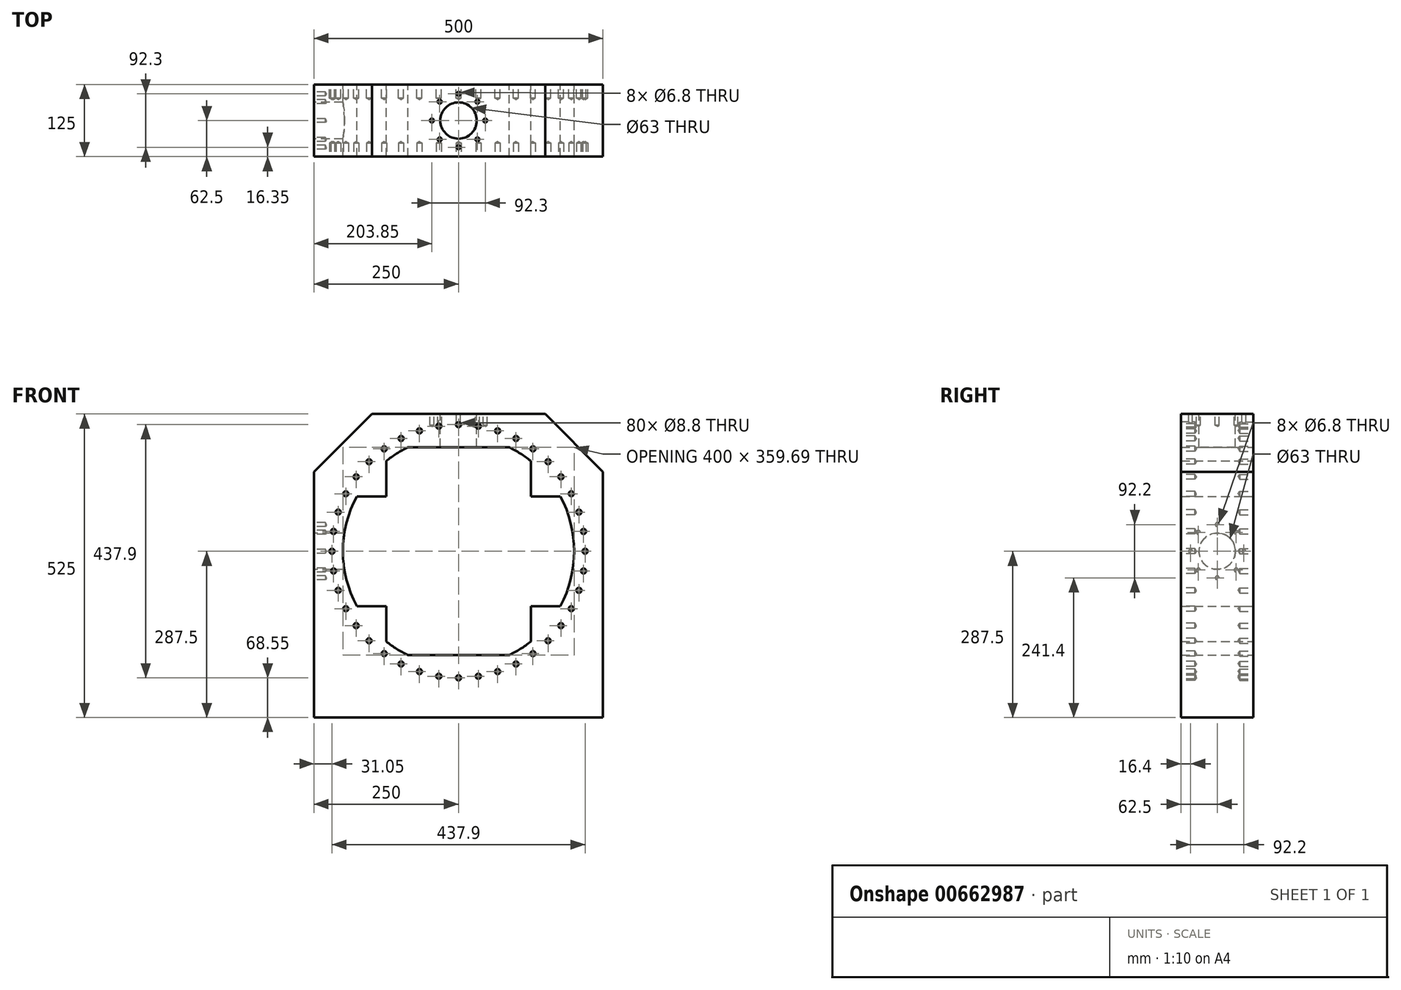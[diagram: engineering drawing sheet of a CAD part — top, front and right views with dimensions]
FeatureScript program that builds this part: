
annotation { "Feature Type Name" : "Feature", "Feature Type Description" : "" }
export const myFeature = defineFeature(function(context is Context, id is Id, definition is map)
    precondition{}
    {
        {
            var Q0;
            Q0=qCreatedBy(makeId("Front.planeOp"),FACE);
            var sketch = newSketch(context, id + "F0", { "sketchPlane" : qUnion([Q0])});
            skPoint(sketch, "E0.middle", {"position": v(0, 0) * mm});
            skLineSegment(sketch, "E1.bottom", {"start": v(250, -287.5) * mm, "end": v(-250, -287.5) * mm});
            skLineSegment(sketch, "E1.top", {"start": v(250, 237.5) * mm, "end": v(-250, 237.5) * mm});
            skLineSegment(sketch, "E1.left", {"start": v(250, -287.5) * mm, "end": v(250, 237.5) * mm});
            skLineSegment(sketch, "E1.right", {"start": v(-250, -287.5) * mm, "end": v(-250, 237.5) * mm});
            skPoint(sketch, "E1.middle", {"position": v(0, -25) * mm});
            skCircle(sketch, "E2", {"center": v(0, 0) * mm, "radius": 235 * mm, "construction": true});
            skLineSegment(sketch, "E3", {"start": v(0, 200) * mm, "end": v(0, -200) * mm, "construction": true});
            skLineSegment(sketch, "E4", {"start": v(-176, 95) * mm, "end": v(-125, 95) * mm});
            skLineSegment(sketch, "E5", {"start": v(-125, 95) * mm, "end": v(-125, 156.12) * mm});
            skLineSegment(sketch, "E6", {"start": v(-125, -95) * mm, "end": v(-176, -95) * mm});
            skLineSegment(sketch, "E7", {"start": v(176, 95) * mm, "end": v(125, 95) * mm});
            skLineSegment(sketch, "E8", {"start": v(125, 95) * mm, "end": v(125, 156.12) * mm});
            skLineSegment(sketch, "E9", {"start": v(176, -95) * mm, "end": v(125, -95) * mm});
            skLineSegment(sketch, "E10", {"start": v(125, -95) * mm, "end": v(125, -156.12) * mm});
            skArc(sketch, "E11", {"start": v(176, 95) * mm, "mid": v(153.57, 128.13) * mm, "end": v(125, 156.12) * mm, "construction": true});
            skArc(sketch, "E12", {"start": v(176, -95) * mm, "mid": v(200, 0) * mm, "end": v(176, 95) * mm});
            skArc(sketch, "E13", {"start": v(125, 156.12) * mm, "mid": v(106.9, 169.03) * mm, "end": v(87.5, 179.84) * mm});
            skArc(sketch, "E14", {"start": v(-125, 156.12) * mm, "mid": v(-153.57, 128.13) * mm, "end": v(-176, 95) * mm, "construction": true});
            skArc(sketch, "E15", {"start": v(-176, 95) * mm, "mid": v(-200, 0) * mm, "end": v(-176, -95) * mm});
            skArc(sketch, "E16", {"start": v(-176, -95) * mm, "mid": v(-153.57, -128.13) * mm, "end": v(-125, -156.12) * mm, "construction": true});
            skLineSegment(sketch, "E17", {"start": v(-87.5, 179.84) * mm, "end": v(87.5, 179.84) * mm});
            skArc(sketch, "E18", {"start": v(-87.5, 179.84) * mm, "mid": v(-106.9, 169.03) * mm, "end": v(-125, 156.12) * mm});
            skLineSegment(sketch, "E19", {"start": v(87.5, 179.84) * mm, "end": v(87.5, 179.84) * mm});
            skArc(sketch, "E20", {"start": v(87.5, 179.84) * mm, "mid": v(0, 200) * mm, "end": v(-87.5, 179.84) * mm, "construction": true});
            skCircle(sketch, "E21", {"center": v(0, 0) * mm, "radius": 218.95 * mm, "construction": true});
            skLineSegment(sketch, "E22", {"start": v(-125, -95) * mm, "end": v(-125, -156.12) * mm});
            skLineSegment(sketch, "E23", {"start": v(-125, -156.12) * mm, "end": v(125, -156.12) * mm, "construction": true});
            skLineSegment(sketch, "E24", {"start": v(-87.5, -179.84) * mm, "end": v(87.5, -179.84) * mm});
            skArc(sketch, "E25", {"start": v(-87.5, -179.84) * mm, "mid": v(0, -200) * mm, "end": v(87.5, -179.84) * mm, "construction": true});
            skArc(sketch, "E26", {"start": v(-125, -156.12) * mm, "mid": v(-106.9, -169.03) * mm, "end": v(-87.5, -179.84) * mm});
            skLineSegment(sketch, "E27", {"start": v(87.5, -179.84) * mm, "end": v(87.5, -179.84) * mm});
            skLineSegment(sketch, "E28", {"start": v(125, -156.12) * mm, "end": v(125, -156.12) * mm});
            skArc(sketch, "E29", {"start": v(87.5, -179.84) * mm, "mid": v(106.9, -169.03) * mm, "end": v(125, -156.12) * mm});
            skPoint(sketch, "E30", {"position": v(218.95, 0) * mm});
            skLineSegment(sketch, "E31", {"start": v(0, 0) * mm, "end": v(218.95, 0) * mm, "construction": true});
            skPoint(sketch, "E32.1.0", {"position": v(216.25, 34.25) * mm});
            skPoint(sketch, "E32.2.0", {"position": v(208.23, 67.66) * mm});
            skPoint(sketch, "E32.3.0", {"position": v(195.09, 99.4) * mm});
            skPoint(sketch, "E32.4.0", {"position": v(177.13, 128.7) * mm});
            skPoint(sketch, "E32.5.0", {"position": v(154.82, 154.82) * mm});
            skPoint(sketch, "E32.6.0", {"position": v(128.7, 177.13) * mm});
            skPoint(sketch, "E32.7.0", {"position": v(99.4, 195.09) * mm});
            skPoint(sketch, "E32.8.0", {"position": v(67.66, 208.23) * mm});
            skPoint(sketch, "E32.9.0", {"position": v(34.25, 216.25) * mm});
            skPoint(sketch, "E32.10.0", {"position": v(0, 218.95) * mm});
            skPoint(sketch, "E32.11.0", {"position": v(-34.25, 216.25) * mm});
            skPoint(sketch, "E32.12.0", {"position": v(-67.66, 208.23) * mm});
            skPoint(sketch, "E32.13.0", {"position": v(-99.4, 195.09) * mm});
            skPoint(sketch, "E32.14.0", {"position": v(-128.7, 177.13) * mm});
            skPoint(sketch, "E32.15.0", {"position": v(-154.82, 154.82) * mm});
            skPoint(sketch, "E32.16.0", {"position": v(-177.13, 128.7) * mm});
            skPoint(sketch, "E32.17.0", {"position": v(-195.09, 99.4) * mm});
            skPoint(sketch, "E32.18.0", {"position": v(-208.23, 67.66) * mm});
            skPoint(sketch, "E32.19.0", {"position": v(-216.25, 34.25) * mm});
            skPoint(sketch, "E32.20.0", {"position": v(-218.95, 0) * mm});
            skPoint(sketch, "E32.21.0", {"position": v(-216.25, -34.25) * mm});
            skPoint(sketch, "E32.22.0", {"position": v(-208.23, -67.66) * mm});
            skPoint(sketch, "E32.23.0", {"position": v(-195.09, -99.4) * mm});
            skPoint(sketch, "E32.24.0", {"position": v(-177.13, -128.7) * mm});
            skPoint(sketch, "E32.25.0", {"position": v(-154.82, -154.82) * mm});
            skPoint(sketch, "E32.26.0", {"position": v(-128.7, -177.13) * mm});
            skPoint(sketch, "E32.27.0", {"position": v(-99.4, -195.09) * mm});
            skPoint(sketch, "E32.28.0", {"position": v(-67.66, -208.23) * mm});
            skPoint(sketch, "E32.29.0", {"position": v(-34.25, -216.25) * mm});
            skPoint(sketch, "E32.30.0", {"position": v(0, -218.95) * mm});
            skPoint(sketch, "E32.31.0", {"position": v(34.25, -216.25) * mm});
            skPoint(sketch, "E32.32.0", {"position": v(67.66, -208.23) * mm});
            skPoint(sketch, "E32.33.0", {"position": v(99.4, -195.09) * mm});
            skPoint(sketch, "E32.34.0", {"position": v(128.7, -177.13) * mm});
            skPoint(sketch, "E32.35.0", {"position": v(154.82, -154.82) * mm});
            skPoint(sketch, "E32.36.0", {"position": v(177.13, -128.7) * mm});
            skPoint(sketch, "E32.37.0", {"position": v(195.09, -99.4) * mm});
            skPoint(sketch, "E32.38.0", {"position": v(208.23, -67.66) * mm});
            skPoint(sketch, "E32.39.0", {"position": v(216.25, -34.25) * mm});
            skSolve(sketch);
        }
        {
            var Q0;
            Q0=makeQuery(id+"F0.imprint","IMPRINT",FACE,{"disambiguationData":[TD([[makeQuery(id+"F0.imprint","IMPRINT",EDGE,{"derivedFrom":sQuery(id+"F0.wireOp",EDGE,"E1.bottom")}),-1.0]])]});
            extrude(context, id + "F1", {"entities" : qUnion([Q0]), "depth" : 125 * mm, "offsetDistance" : 25 * mm});
        }
        {
            var Q0;
            Q0=sQuery(id+"F0.wireOp",VERTEX,"E32.20.0");
            var Q1;
            Q1=sQuery(id+"F0.wireOp",VERTEX,"E32.19.0");
            var Q2;
            Q2=sQuery(id+"F0.wireOp",VERTEX,"E32.18.0");
            var Q3;
            Q3=sQuery(id+"F0.wireOp",VERTEX,"E32.17.0");
            var Q4;
            Q4=sQuery(id+"F0.wireOp",VERTEX,"E32.16.0");
            var Q5;
            Q5=sQuery(id+"F0.wireOp",VERTEX,"E32.15.0");
            var Q6;
            Q6=sQuery(id+"F0.wireOp",VERTEX,"E32.14.0");
            var Q7;
            Q7=sQuery(id+"F0.wireOp",VERTEX,"E32.13.0");
            var Q8;
            Q8=sQuery(id+"F0.wireOp",VERTEX,"E32.12.0");
            var Q9;
            Q9=sQuery(id+"F0.wireOp",VERTEX,"E32.11.0");
            var Q10;
            Q10=sQuery(id+"F0.wireOp",VERTEX,"E32.10.0");
            var Q11;
            Q11=sQuery(id+"F0.wireOp",VERTEX,"E32.9.0");
            var Q12;
            Q12=sQuery(id+"F0.wireOp",VERTEX,"E32.8.0");
            var Q13;
            Q13=sQuery(id+"F0.wireOp",VERTEX,"E32.7.0");
            var Q14;
            Q14=sQuery(id+"F0.wireOp",VERTEX,"E32.6.0");
            var Q15;
            Q15=sQuery(id+"F0.wireOp",VERTEX,"E32.5.0");
            var Q16;
            Q16=sQuery(id+"F0.wireOp",VERTEX,"E32.4.0");
            var Q17;
            Q17=sQuery(id+"F0.wireOp",VERTEX,"E32.3.0");
            var Q18;
            Q18=sQuery(id+"F0.wireOp",VERTEX,"E32.2.0");
            var Q19;
            Q19=sQuery(id+"F0.wireOp",VERTEX,"E32.1.0");
            var Q20;
            Q20=sQuery(id+"F0.wireOp",VERTEX,"E30");
            var Q21;
            Q21=sQuery(id+"F0.wireOp",VERTEX,"E32.39.0");
            var Q22;
            Q22=sQuery(id+"F0.wireOp",VERTEX,"E32.38.0");
            var Q23;
            Q23=sQuery(id+"F0.wireOp",VERTEX,"E32.37.0");
            var Q24;
            Q24=sQuery(id+"F0.wireOp",VERTEX,"E32.36.0");
            var Q25;
            Q25=sQuery(id+"F0.wireOp",VERTEX,"E32.35.0");
            var Q26;
            Q26=sQuery(id+"F0.wireOp",VERTEX,"E32.34.0");
            var Q27;
            Q27=sQuery(id+"F0.wireOp",VERTEX,"E32.33.0");
            var Q28;
            Q28=sQuery(id+"F0.wireOp",VERTEX,"E32.32.0");
            var Q29;
            Q29=sQuery(id+"F0.wireOp",VERTEX,"E32.31.0");
            var Q30;
            Q30=sQuery(id+"F0.wireOp",VERTEX,"E32.30.0");
            var Q31;
            Q31=sQuery(id+"F0.wireOp",VERTEX,"E32.29.0");
            var Q32;
            Q32=sQuery(id+"F0.wireOp",VERTEX,"E32.28.0");
            var Q33;
            Q33=sQuery(id+"F0.wireOp",VERTEX,"E32.27.0");
            var Q34;
            Q34=sQuery(id+"F0.wireOp",VERTEX,"E32.26.0");
            var Q35;
            Q35=sQuery(id+"F0.wireOp",VERTEX,"E32.25.0");
            var Q36;
            Q36=sQuery(id+"F0.wireOp",VERTEX,"E32.24.0");
            var Q37;
            Q37=sQuery(id+"F0.wireOp",VERTEX,"E32.23.0");
            var Q38;
            Q38=sQuery(id+"F0.wireOp",VERTEX,"E32.22.0");
            var Q39;
            Q39=sQuery(id+"F0.wireOp",VERTEX,"E32.21.0");
            var Q40;
            Q40=makeQuery(id+"F1.opExtrude","SWEPT_BODY",BODY,{"disambiguationData":[OSD([sQuery(id+"F0.wireOp",EDGE,"E1.bottom"),sQuery(id+"F0.wireOp",EDGE,"E1.top"),sQuery(id+"F0.wireOp",EDGE,"E1.left"),sQuery(id+"F0.wireOp",EDGE,"E1.right"),sQuery(id+"F0.wireOp",EDGE,"E4"),sQuery(id+"F0.wireOp",EDGE,"E5"),sQuery(id+"F0.wireOp",EDGE,"E6"),sQuery(id+"F0.wireOp",EDGE,"E7"),sQuery(id+"F0.wireOp",EDGE,"E8"),sQuery(id+"F0.wireOp",EDGE,"E9"),sQuery(id+"F0.wireOp",EDGE,"E10"),sQuery(id+"F0.wireOp",EDGE,"E12"),sQuery(id+"F0.wireOp",EDGE,"E13"),sQuery(id+"F0.wireOp",EDGE,"E15"),sQuery(id+"F0.wireOp",EDGE,"E17"),sQuery(id+"F0.wireOp",EDGE,"E18"),sQuery(id+"F0.wireOp",EDGE,"E22"),sQuery(id+"F0.wireOp",EDGE,"E24"),sQuery(id+"F0.wireOp",EDGE,"E26"),sQuery(id+"F0.wireOp",EDGE,"E29")])]});
            hole(context, id + "F2", {"style" : HoleStyle.SIMPLE, "endStyle" : HoleEndStyle.BLIND, "oppositeDirection" : true, "standardTappedOrClearance" : lookupTablePath({ "standard" : "ISO", "engagement" : "75%", "pitch" : "1.25 mm", "size" : "M10", "type" : "Tapped" }), "standardBlindInLast" : lookupTablePath({ "standard" : "ISO", "fit" : "Normal", "engagement" : "75%", "pitch" : "1.25 mm", "size" : "M10", "type" : "Clearance & tapped" }), "holeDiameter" : 8.8 * mm, "majorDiameter" : 10 * mm, "showTappedDepth" : true, "holeDepth" : 23.75 * mm, "isTappedThrough" : true, "tappedDepth" : 20 * mm, "tapClearance" : 3, "locations" : qUnion([Q0, Q1, Q2, Q3, Q4, Q5, Q6, Q7, Q8, Q9, Q10, Q11, Q12, Q13, Q14, Q15, Q16, Q17, Q18, Q19, Q20, Q21, Q22, Q23, Q24, Q25, Q26, Q27, Q28, Q29, Q30, Q31, Q32, Q33, Q34, Q35, Q36, Q37, Q38, Q39]), "scope" : qUnion([Q40])});
        }
        {
            var Q0;
            Q0=makeQuery(id+"F1.opExtrude","SWEPT_EDGE",EDGE,{"disambiguationData":[OSD([sQuery(id+"F0.wireOp",EDGE,"E1.top"),sQuery(id+"F0.wireOp",EDGE,"E1.right")])]});
            var Q1;
            Q1=makeQuery(id+"F1.opExtrude","SWEPT_EDGE",EDGE,{"disambiguationData":[OSD([sQuery(id+"F0.wireOp",EDGE,"E1.top"),sQuery(id+"F0.wireOp",EDGE,"E1.left")])]});
            chamfer(context, id + "F3", {"entities" : qUnion([Q0, Q1]), "width" : 100 * mm, "tangentPropagation" : true});
        }
        {
            var Q0;
            Q0=makeQuery(id+"F1.opExtrude","CAP_FACE",FACE,{"disambiguationData":[OSD([sQuery(id+"F0.wireOp",EDGE,"E1.bottom"),sQuery(id+"F0.wireOp",EDGE,"E1.top"),sQuery(id+"F0.wireOp",EDGE,"E1.left"),sQuery(id+"F0.wireOp",EDGE,"E1.right"),sQuery(id+"F0.wireOp",EDGE,"E4"),sQuery(id+"F0.wireOp",EDGE,"E5"),sQuery(id+"F0.wireOp",EDGE,"E6"),sQuery(id+"F0.wireOp",EDGE,"E7"),sQuery(id+"F0.wireOp",EDGE,"E8"),sQuery(id+"F0.wireOp",EDGE,"E9"),sQuery(id+"F0.wireOp",EDGE,"E10"),sQuery(id+"F0.wireOp",EDGE,"E12"),sQuery(id+"F0.wireOp",EDGE,"E13"),sQuery(id+"F0.wireOp",EDGE,"E15"),sQuery(id+"F0.wireOp",EDGE,"E17"),sQuery(id+"F0.wireOp",EDGE,"E18"),sQuery(id+"F0.wireOp",EDGE,"E22"),sQuery(id+"F0.wireOp",EDGE,"E24"),sQuery(id+"F0.wireOp",EDGE,"E26"),sQuery(id+"F0.wireOp",EDGE,"E29")])],"isStart":false});
            var sketch = newSketch(context, id + "F4", { "sketchPlane" : qUnion([Q0])});
            skCircle(sketch, "E33", {"center": v(0, 0) * mm, "radius": 218.95 * mm, "construction": true});
            skPoint(sketch, "E34", {"position": v(218.95, 0) * mm});
            skLineSegment(sketch, "E35", {"start": v(0, 0) * mm, "end": v(218.95, 0) * mm, "construction": true});
            skPoint(sketch, "E36.1.0", {"position": v(216.25, 34.25) * mm});
            skPoint(sketch, "E36.2.0", {"position": v(208.23, 67.66) * mm});
            skPoint(sketch, "E36.3.0", {"position": v(195.09, 99.4) * mm});
            skPoint(sketch, "E36.4.0", {"position": v(177.13, 128.7) * mm});
            skPoint(sketch, "E36.5.0", {"position": v(154.82, 154.82) * mm});
            skPoint(sketch, "E36.6.0", {"position": v(128.7, 177.13) * mm});
            skPoint(sketch, "E36.7.0", {"position": v(99.4, 195.09) * mm});
            skPoint(sketch, "E36.8.0", {"position": v(67.66, 208.23) * mm});
            skPoint(sketch, "E36.9.0", {"position": v(34.25, 216.25) * mm});
            skPoint(sketch, "E36.10.0", {"position": v(0, 218.95) * mm});
            skPoint(sketch, "E36.11.0", {"position": v(-34.25, 216.25) * mm});
            skPoint(sketch, "E36.12.0", {"position": v(-67.66, 208.23) * mm});
            skPoint(sketch, "E36.13.0", {"position": v(-99.4, 195.09) * mm});
            skPoint(sketch, "E36.14.0", {"position": v(-128.7, 177.13) * mm});
            skPoint(sketch, "E36.15.0", {"position": v(-154.82, 154.82) * mm});
            skPoint(sketch, "E36.16.0", {"position": v(-177.13, 128.7) * mm});
            skPoint(sketch, "E36.17.0", {"position": v(-195.09, 99.4) * mm});
            skPoint(sketch, "E36.18.0", {"position": v(-208.23, 67.66) * mm});
            skPoint(sketch, "E36.19.0", {"position": v(-216.25, 34.25) * mm});
            skPoint(sketch, "E36.20.0", {"position": v(-218.95, 0) * mm});
            skPoint(sketch, "E36.21.0", {"position": v(-216.25, -34.25) * mm});
            skPoint(sketch, "E36.22.0", {"position": v(-208.23, -67.66) * mm});
            skPoint(sketch, "E36.23.0", {"position": v(-195.09, -99.4) * mm});
            skPoint(sketch, "E36.24.0", {"position": v(-177.13, -128.7) * mm});
            skPoint(sketch, "E36.25.0", {"position": v(-154.82, -154.82) * mm});
            skPoint(sketch, "E36.26.0", {"position": v(-128.7, -177.13) * mm});
            skPoint(sketch, "E36.27.0", {"position": v(-99.4, -195.09) * mm});
            skPoint(sketch, "E36.28.0", {"position": v(-67.66, -208.23) * mm});
            skPoint(sketch, "E36.29.0", {"position": v(-34.25, -216.25) * mm});
            skPoint(sketch, "E36.30.0", {"position": v(0, -218.95) * mm});
            skPoint(sketch, "E36.31.0", {"position": v(34.25, -216.25) * mm});
            skPoint(sketch, "E36.32.0", {"position": v(67.66, -208.23) * mm});
            skPoint(sketch, "E36.33.0", {"position": v(99.4, -195.09) * mm});
            skPoint(sketch, "E36.34.0", {"position": v(128.7, -177.13) * mm});
            skPoint(sketch, "E36.35.0", {"position": v(154.82, -154.82) * mm});
            skPoint(sketch, "E36.36.0", {"position": v(177.13, -128.7) * mm});
            skPoint(sketch, "E36.37.0", {"position": v(195.09, -99.4) * mm});
            skPoint(sketch, "E36.38.0", {"position": v(208.23, -67.66) * mm});
            skPoint(sketch, "E36.39.0", {"position": v(216.25, -34.25) * mm});
            skSolve(sketch);
        }
        {
            var Q0;
            Q0=sQuery(id+"F4.wireOp",VERTEX,"E34");
            var Q1;
            Q1=sQuery(id+"F4.wireOp",VERTEX,"E36.1.0");
            var Q2;
            Q2=sQuery(id+"F4.wireOp",VERTEX,"E36.2.0");
            var Q3;
            Q3=sQuery(id+"F4.wireOp",VERTEX,"E36.3.0");
            var Q4;
            Q4=sQuery(id+"F4.wireOp",VERTEX,"E36.4.0");
            var Q5;
            Q5=sQuery(id+"F4.wireOp",VERTEX,"E36.5.0");
            var Q6;
            Q6=sQuery(id+"F4.wireOp",VERTEX,"E36.6.0");
            var Q7;
            Q7=sQuery(id+"F4.wireOp",VERTEX,"E36.7.0");
            var Q8;
            Q8=sQuery(id+"F4.wireOp",VERTEX,"E36.8.0");
            var Q9;
            Q9=sQuery(id+"F4.wireOp",VERTEX,"E36.9.0");
            var Q10;
            Q10=sQuery(id+"F4.wireOp",VERTEX,"E36.10.0");
            var Q11;
            Q11=sQuery(id+"F4.wireOp",VERTEX,"E36.11.0");
            var Q12;
            Q12=sQuery(id+"F4.wireOp",VERTEX,"E36.12.0");
            var Q13;
            Q13=sQuery(id+"F4.wireOp",VERTEX,"E36.13.0");
            var Q14;
            Q14=sQuery(id+"F4.wireOp",VERTEX,"E36.14.0");
            var Q15;
            Q15=sQuery(id+"F4.wireOp",VERTEX,"E36.15.0");
            var Q16;
            Q16=sQuery(id+"F4.wireOp",VERTEX,"E36.16.0");
            var Q17;
            Q17=sQuery(id+"F4.wireOp",VERTEX,"E36.17.0");
            var Q18;
            Q18=sQuery(id+"F4.wireOp",VERTEX,"E36.18.0");
            var Q19;
            Q19=sQuery(id+"F4.wireOp",VERTEX,"E36.19.0");
            var Q20;
            Q20=sQuery(id+"F4.wireOp",VERTEX,"E36.20.0");
            var Q21;
            Q21=sQuery(id+"F4.wireOp",VERTEX,"E36.21.0");
            var Q22;
            Q22=sQuery(id+"F4.wireOp",VERTEX,"E36.22.0");
            var Q23;
            Q23=sQuery(id+"F4.wireOp",VERTEX,"E36.23.0");
            var Q24;
            Q24=sQuery(id+"F4.wireOp",VERTEX,"E36.24.0");
            var Q25;
            Q25=sQuery(id+"F4.wireOp",VERTEX,"E36.25.0");
            var Q26;
            Q26=sQuery(id+"F4.wireOp",VERTEX,"E36.26.0");
            var Q27;
            Q27=sQuery(id+"F4.wireOp",VERTEX,"E36.27.0");
            var Q28;
            Q28=sQuery(id+"F4.wireOp",VERTEX,"E36.28.0");
            var Q29;
            Q29=sQuery(id+"F4.wireOp",VERTEX,"E36.29.0");
            var Q30;
            Q30=sQuery(id+"F4.wireOp",VERTEX,"E36.30.0");
            var Q31;
            Q31=sQuery(id+"F4.wireOp",VERTEX,"E36.31.0");
            var Q32;
            Q32=sQuery(id+"F4.wireOp",VERTEX,"E36.32.0");
            var Q33;
            Q33=sQuery(id+"F4.wireOp",VERTEX,"E36.33.0");
            var Q34;
            Q34=sQuery(id+"F4.wireOp",VERTEX,"E36.34.0");
            var Q35;
            Q35=sQuery(id+"F4.wireOp",VERTEX,"E36.35.0");
            var Q36;
            Q36=sQuery(id+"F4.wireOp",VERTEX,"E36.36.0");
            var Q37;
            Q37=sQuery(id+"F4.wireOp",VERTEX,"E36.37.0");
            var Q38;
            Q38=sQuery(id+"F4.wireOp",VERTEX,"E36.38.0");
            var Q39;
            Q39=sQuery(id+"F4.wireOp",VERTEX,"E36.39.0");
            var Q40;
            Q40=makeQuery(id+"F1.opExtrude","SWEPT_BODY",BODY,{"disambiguationData":[OSD([sQuery(id+"F0.wireOp",EDGE,"E1.bottom"),sQuery(id+"F0.wireOp",EDGE,"E1.top"),sQuery(id+"F0.wireOp",EDGE,"E1.left"),sQuery(id+"F0.wireOp",EDGE,"E1.right"),sQuery(id+"F0.wireOp",EDGE,"E4"),sQuery(id+"F0.wireOp",EDGE,"E5"),sQuery(id+"F0.wireOp",EDGE,"E6"),sQuery(id+"F0.wireOp",EDGE,"E7"),sQuery(id+"F0.wireOp",EDGE,"E8"),sQuery(id+"F0.wireOp",EDGE,"E9"),sQuery(id+"F0.wireOp",EDGE,"E10"),sQuery(id+"F0.wireOp",EDGE,"E12"),sQuery(id+"F0.wireOp",EDGE,"E13"),sQuery(id+"F0.wireOp",EDGE,"E15"),sQuery(id+"F0.wireOp",EDGE,"E17"),sQuery(id+"F0.wireOp",EDGE,"E18"),sQuery(id+"F0.wireOp",EDGE,"E22"),sQuery(id+"F0.wireOp",EDGE,"E24"),sQuery(id+"F0.wireOp",EDGE,"E26"),sQuery(id+"F0.wireOp",EDGE,"E29")])]});
            hole(context, id + "F5", {"style" : HoleStyle.SIMPLE, "endStyle" : HoleEndStyle.BLIND, "standardTappedOrClearance" : lookupTablePath({ "standard" : "ISO", "engagement" : "75%", "pitch" : "1.25 mm", "size" : "M10", "type" : "Tapped" }), "standardBlindInLast" : lookupTablePath({ "fit" : "Normal", "standard" : "ISO", "engagement" : "75%", "pitch" : "1.25 mm", "size" : "M10", "type" : "Clearance & tapped" }), "holeDiameter" : 8.8 * mm, "majorDiameter" : 10 * mm, "showTappedDepth" : true, "holeDepth" : 23.75 * mm, "isTappedThrough" : true, "tappedDepth" : 20 * mm, "tapClearance" : 3, "locations" : qUnion([Q0, Q1, Q2, Q3, Q4, Q5, Q6, Q7, Q8, Q9, Q10, Q11, Q12, Q13, Q14, Q15, Q16, Q17, Q18, Q19, Q20, Q21, Q22, Q23, Q24, Q25, Q26, Q27, Q28, Q29, Q30, Q31, Q32, Q33, Q34, Q35, Q36, Q37, Q38, Q39]), "scope" : qUnion([Q40])});
        }
        {
            var Q0;
            Q0=makeQuery(id+"F1.opExtrude","SWEPT_FACE",FACE,{"disambiguationData":[OSD([sQuery(id+"F0.wireOp",EDGE,"E1.top")])]});
            var sketch = newSketch(context, id + "F6", { "sketchPlane" : qUnion([Q0])});
            skCircle(sketch, "E37", {"center": v(0, -62.5) * mm, "radius": 31.5 * mm});
            skPoint(sketch, "E37.centerSnap0", {"position": v(150, -62.5) * mm});
            skPoint(sketch, "E37.centerSnap1", {"position": v(0, 0) * mm});
            skCircle(sketch, "E38", {"center": v(0, -62.5) * mm, "radius": 46.15 * mm, "construction": true});
            skPoint(sketch, "E39", {"position": v(46.15, -62.5) * mm});
            skLineSegment(sketch, "E40", {"start": v(0, -62.5) * mm, "end": v(46.15, -62.5) * mm, "construction": true});
            skPoint(sketch, "E41.1.0", {"position": v(32.63, -29.87) * mm});
            skPoint(sketch, "E41.2.0", {"position": v(0, -16.35) * mm});
            skPoint(sketch, "E41.3.0", {"position": v(-32.63, -29.87) * mm});
            skPoint(sketch, "E41.4.0", {"position": v(-46.15, -62.5) * mm});
            skPoint(sketch, "E41.5.0", {"position": v(-32.63, -95.13) * mm});
            skPoint(sketch, "E41.6.0", {"position": v(0, -108.65) * mm});
            skPoint(sketch, "E41.7.0", {"position": v(32.63, -95.13) * mm});
            skSolve(sketch);
        }
        {
            var Q0;
            Q0=makeQuery(id+"F6.imprint","IMPRINT",FACE,{"disambiguationData":[TD([[makeQuery(id+"F6.imprint","IMPRINT",EDGE,{"derivedFrom":sQuery(id+"F6.wireOp",EDGE,"E37")}),1.0]])]});
            var Q1;
            Q1=makeQuery(id+"F1.opExtrude","SWEPT_FACE",FACE,{"disambiguationData":[OSD([sQuery(id+"F0.wireOp",EDGE,"E17")])]});
            extrude(context, id + "F7", {"entities" : qUnion([Q0]), "operationType" : NewBodyOperationType.REMOVE, "endBound" : BoundingType.UP_TO_SURFACE, "oppositeDirection" : true, "depth" : 25 * mm, "endBoundEntityFace" : qUnion([Q1]), "offsetDistance" : 25 * mm});
        }
        {
            var Q0;
            Q0=sQuery(id+"F6.wireOp",VERTEX,"E39");
            var Q1;
            Q1=sQuery(id+"F6.wireOp",VERTEX,"E41.7.0");
            var Q2;
            Q2=sQuery(id+"F6.wireOp",VERTEX,"E41.6.0");
            var Q3;
            Q3=sQuery(id+"F6.wireOp",VERTEX,"E41.5.0");
            var Q4;
            Q4=sQuery(id+"F6.wireOp",VERTEX,"E41.4.0");
            var Q5;
            Q5=sQuery(id+"F6.wireOp",VERTEX,"E41.3.0");
            var Q6;
            Q6=sQuery(id+"F6.wireOp",VERTEX,"E41.2.0");
            var Q7;
            Q7=sQuery(id+"F6.wireOp",VERTEX,"E41.1.0");
            var Q8;
            Q8=makeQuery(id+"F1.opExtrude","SWEPT_BODY",BODY,{"disambiguationData":[OSD([sQuery(id+"F0.wireOp",EDGE,"E1.bottom"),sQuery(id+"F0.wireOp",EDGE,"E1.top"),sQuery(id+"F0.wireOp",EDGE,"E1.left"),sQuery(id+"F0.wireOp",EDGE,"E1.right"),sQuery(id+"F0.wireOp",EDGE,"E4"),sQuery(id+"F0.wireOp",EDGE,"E5"),sQuery(id+"F0.wireOp",EDGE,"E6"),sQuery(id+"F0.wireOp",EDGE,"E7"),sQuery(id+"F0.wireOp",EDGE,"E8"),sQuery(id+"F0.wireOp",EDGE,"E9"),sQuery(id+"F0.wireOp",EDGE,"E10"),sQuery(id+"F0.wireOp",EDGE,"E12"),sQuery(id+"F0.wireOp",EDGE,"E13"),sQuery(id+"F0.wireOp",EDGE,"E15"),sQuery(id+"F0.wireOp",EDGE,"E17"),sQuery(id+"F0.wireOp",EDGE,"E18"),sQuery(id+"F0.wireOp",EDGE,"E22"),sQuery(id+"F0.wireOp",EDGE,"E24"),sQuery(id+"F0.wireOp",EDGE,"E26"),sQuery(id+"F0.wireOp",EDGE,"E29")])]});
            hole(context, id + "F8", {"style" : HoleStyle.SIMPLE, "endStyle" : HoleEndStyle.BLIND, "standardTappedOrClearance" : lookupTablePath({ "standard" : "ISO", "engagement" : "75%", "pitch" : "1.25 mm", "size" : "M8", "type" : "Tapped" }), "standardBlindInLast" : lookupTablePath({ "standard" : "ISO", "fit" : "Normal", "engagement" : "75%", "pitch" : "1.25 mm", "size" : "M8", "type" : "Clearance & tapped" }), "holeDiameter" : 6.8 * mm, "majorDiameter" : 8 * mm, "showTappedDepth" : true, "holeDepth" : 19.75 * mm, "isTappedThrough" : true, "tappedDepth" : 16 * mm, "tapClearance" : 3, "locations" : qUnion([Q0, Q1, Q2, Q3, Q4, Q5, Q6, Q7]), "scope" : qUnion([Q8])});
        }
        {
            var Q0;
            Q0=makeQuery(id+"F1.opExtrude","SWEPT_FACE",FACE,{"disambiguationData":[OSD([sQuery(id+"F0.wireOp",EDGE,"E1.right")])]});
            var sketch = newSketch(context, id + "F9", { "sketchPlane" : qUnion([Q0])});
            skCircle(sketch, "E42", {"center": v(62.5, 0) * mm, "radius": 31.5 * mm});
            skPoint(sketch, "E42.centerSnap0", {"position": v(62.5, 137.5) * mm});
            skCircle(sketch, "E43", {"center": v(62.5, 0) * mm, "radius": 46.1 * mm, "construction": true});
            skPoint(sketch, "E44", {"position": v(62.5, 46.1) * mm});
            skLineSegment(sketch, "E45", {"start": v(62.5, 0) * mm, "end": v(62.5, 46.1) * mm, "construction": true});
            skLineSegment(sketch, "E46", {"start": v(62.5, 46.1) * mm, "end": v(62.5, 0) * mm, "construction": true});
            skPoint(sketch, "E47.1.0", {"position": v(29.9, 32.6) * mm});
            skPoint(sketch, "E47.2.0", {"position": v(16.4, 0) * mm});
            skPoint(sketch, "E47.3.0", {"position": v(29.9, -32.6) * mm});
            skPoint(sketch, "E47.4.0", {"position": v(62.5, -46.1) * mm});
            skPoint(sketch, "E47.5.0", {"position": v(95.1, -32.6) * mm});
            skPoint(sketch, "E47.6.0", {"position": v(108.6, 0) * mm});
            skPoint(sketch, "E47.7.0", {"position": v(95.1, 32.6) * mm});
            skSolve(sketch);
        }
        {
            var Q0;
            Q0=makeQuery(id+"F9.imprint","IMPRINT",FACE,{"disambiguationData":[TD([[makeQuery(id+"F9.imprint","IMPRINT",EDGE,{"derivedFrom":sQuery(id+"F9.wireOp",EDGE,"E42")}),1.0]])]});
            var Q1;
            Q1=makeQuery(id+"F1.opExtrude","SWEPT_FACE",FACE,{"disambiguationData":[OSD([sQuery(id+"F0.wireOp",EDGE,"E15")])]});
            extrude(context, id + "F10", {"entities" : qUnion([Q0]), "operationType" : NewBodyOperationType.REMOVE, "endBound" : BoundingType.UP_TO_SURFACE, "oppositeDirection" : true, "depth" : 25 * mm, "endBoundEntityFace" : qUnion([Q1]), "offsetDistance" : 25 * mm});
        }
        {
            var Q0;
            Q0=sQuery(id+"F9.wireOp",VERTEX,"E44");
            var Q1;
            Q1=sQuery(id+"F9.wireOp",VERTEX,"E47.7.0");
            var Q2;
            Q2=sQuery(id+"F9.wireOp",VERTEX,"E47.6.0");
            var Q3;
            Q3=sQuery(id+"F9.wireOp",VERTEX,"E47.5.0");
            var Q4;
            Q4=sQuery(id+"F9.wireOp",VERTEX,"E47.4.0");
            var Q5;
            Q5=sQuery(id+"F9.wireOp",VERTEX,"E47.3.0");
            var Q6;
            Q6=sQuery(id+"F9.wireOp",VERTEX,"E47.2.0");
            var Q7;
            Q7=sQuery(id+"F9.wireOp",VERTEX,"E47.1.0");
            var Q8;
            Q8=makeQuery(id+"F1.opExtrude","SWEPT_BODY",BODY,{"disambiguationData":[OSD([sQuery(id+"F0.wireOp",EDGE,"E1.bottom"),sQuery(id+"F0.wireOp",EDGE,"E1.top"),sQuery(id+"F0.wireOp",EDGE,"E1.left"),sQuery(id+"F0.wireOp",EDGE,"E1.right"),sQuery(id+"F0.wireOp",EDGE,"E4"),sQuery(id+"F0.wireOp",EDGE,"E5"),sQuery(id+"F0.wireOp",EDGE,"E6"),sQuery(id+"F0.wireOp",EDGE,"E7"),sQuery(id+"F0.wireOp",EDGE,"E8"),sQuery(id+"F0.wireOp",EDGE,"E9"),sQuery(id+"F0.wireOp",EDGE,"E10"),sQuery(id+"F0.wireOp",EDGE,"E12"),sQuery(id+"F0.wireOp",EDGE,"E13"),sQuery(id+"F0.wireOp",EDGE,"E15"),sQuery(id+"F0.wireOp",EDGE,"E17"),sQuery(id+"F0.wireOp",EDGE,"E18"),sQuery(id+"F0.wireOp",EDGE,"E22"),sQuery(id+"F0.wireOp",EDGE,"E24"),sQuery(id+"F0.wireOp",EDGE,"E26"),sQuery(id+"F0.wireOp",EDGE,"E29")])]});
            hole(context, id + "F11", {"style" : HoleStyle.SIMPLE, "endStyle" : HoleEndStyle.BLIND, "standardTappedOrClearance" : lookupTablePath({ "standard" : "ISO", "engagement" : "75%", "pitch" : "1.25 mm", "size" : "M8", "type" : "Tapped" }), "standardBlindInLast" : lookupTablePath({ "fit" : "Normal", "standard" : "ISO", "engagement" : "75%", "pitch" : "1.25 mm", "size" : "M8", "type" : "Clearance & tapped" }), "holeDiameter" : 6.8 * mm, "majorDiameter" : 8 * mm, "showTappedDepth" : true, "holeDepth" : 19.75 * mm, "isTappedThrough" : true, "tappedDepth" : 16 * mm, "tapClearance" : 3, "locations" : qUnion([Q0, Q1, Q2, Q3, Q4, Q5, Q6, Q7]), "scope" : qUnion([Q8])});
        }
    });
